# Revit family: CA_DWDI_CCW_BHD
name_source: partatom
category: Mechanical Equipment
units: mm (PartAtom-declared; Revit-internal decimal feet)

## family parameters
Always vertical = Yes
Cut with Voids When Loaded = No
OmniClass Number = 23.75.35.17
OmniClass Title = Fans
Part Type = Normal
Room Calculation Point = No
Round Connector Dimension = Use Radius
Shared = No
Work Plane-Based = No

## types (60) — shared parameters
0 = 0"
1" = 1"
1.5 = 1 1/2"
2" = 2"
2' = 24"
3" = 3"
4" = 4"
Manufacturer = Loren Cook Company
Model = CA DWDI
ONE EIGTH = 1/8"
URL = www.lorencook.com

## per-type parameters (varying)
- 120_CA-DWDI_CCW_BHD_CLASS_1: ((B+.25")/2)=8 31/32"; (D-A-.25")/2=1 9/16"; (G/5*3)+2"=10 1/16"; (M-(B+.25"))/2=1 7/8"; -((B+.25")/2)=-8 31/32"; -P=-28 11/16"; A=12 1/8"; A+.25"=12 3/8"; A/2=6 1/16"; B=17 11/16"; B+.25"=17 15/16"; B/2=8 27/32"; BHD_L=2 15/16"; D=15 1/2"; D/2=7 3/4"; E=21 1/16"; E/2=10 17/32"; F=25 3/4"; F-((D-A)/2)=24 1/16"; G=16"; G+((G/5*3)+2")=34 1/8"; G-(G/5*3)=1/4"; G-2.5"=14 9/16"; G/10*3=4 1/32"; G/5*3=8 1/16"; H=24 1/2"; H-1.5=23"; INLET=16 1/8"; INLET/2=8 1/16"; J=12 3/8"; K=22 1/2"; L=10 27/32"; M=21 11/16"; M/2=10 27/32"; N=5 3/4"; P=28 11/16"; P-N=-22 15/16"; P-N-M=1 1/4"; R=1 7/16"; R+R=2 7/8"; R/2=23/32"; S=19 15/16"; T=9 31/32"; Type Comments=Airfoil Centrifugal Blower Counter-Clockwise Bottom Horizontal Arrangement 3 Class 1; U=7 1/2"; V=18"; W=11/16"; W/2=11/32"; X=21 15/16"; X/2=10 31/32"
- 135_CA-DWDI_CCW_BHD_CLASS_1: ((B+.25")/2)=10 3/32"; (D-A-.25")/2=1 9/16"; (G/5*3)+2"=10 13/16"; (M-(B+.25"))/2=1 7/8"; -((B+.25")/2)=-10 3/32"; -P=-30 15/16"; A=13 5/8"; A+.25"=13 7/8"; A/2=6 13/16"; B=19 15/16"; B+.25"=20 3/16"; B/2=9 31/32"; BHD_L=2 5/16"; D=17"; D/2=8 1/2"; E=23 5/16"; E/2=11 21/32"; F=28"; F-((D-A)/2)=26 5/16"; G=17"; G+((G/5*3)+2")=36 5/8"; G-(G/5*3)=1/4"; G-2.5"=15 9/16"; G/10*3=4 13/32"; G/5*3=8 13/16"; H=27"; H-1.5=25 1/2"; INLET=17 5/8"; INLET/2=8 13/16"; J=13 7/8"; K=25"; L=11 31/32"; M=23 15/16"; M/2=11 31/32"; N=5 3/4"; P=30 15/16"; P-N=-25 3/16"; P-N-M=1 1/4"; R=1 7/16"; R+R=2 7/8"; R/2=23/32"; S=22 3/16"; T=11 3/32"; Type Comments=Airfoil Centrifugal Blower Counter-Clockwise Bottom Horizontal Arrangement 3 Class 1; U=8 1/2"; V=18"; W=11/16"; W/2=11/32"; X=24 3/16"; X/2=12 3/32"
- 150_CA-DWDI_CCW_BHD_CLASS_1: ((B+.25")/2)=11 1/8"; (D-A-.25")/2=1 9/16"; (G/5*3)+2"=11 9/16"; (M-(B+.25"))/2=1 7/8"; -((B+.25")/2)=-11 1/8"; -P=-34 1/4"; A=15 1/4"; A+.25"=15 1/2"; A/2=7 5/8"; B=22"; B+.25"=22 1/4"; B/2=11"; BHD_L=2 11/16"; D=18 5/8"; D/2=9 5/16"; E=25 3/8"; E/2=12 11/16"; F=31 3/16"; F-((D-A)/2)=29 1/2"; G=19"; G+((G/5*3)+2")=40 1/8"; G-(G/5*3)=1/4"; G-2.5"=17 5/16"; G/10*3=4 25/32"; G/5*3=9 9/16"; H=29"; H-1.5=27 1/2"; INLET=19 1/8"; INLET/2=9 9/16"; J=15 3/16"; K=26 7/8"; L=13"; M=26"; M/2=13"; N=6 5/8"; P=34 1/4"; P-N=-27 5/8"; P-N-M=1 5/8"; R=1 11/16"; R+R=3 3/8"; R/2=27/32"; S=24 1/4"; T=12 1/8"; Type Comments=Airfoil Centrifugal Blower Counter-Clockwise Bottom Horizontal Arrangement 3 Class 1; U=9"; V=18"; W=11/16"; W/2=11/32"; X=26 1/4"; X/2=13 1/8"
- 165_CA-DWDI_CCW_BHD_CLASS_1: ((B+.25")/2)=12 1/8"; (D-A-.25")/2=1 9/16"; (G/5*3)+2"=12 19/32"; (M-(B+.25"))/2=1 7/8"; -((B+.25")/2)=-12 1/8"; -P=-36 1/4"; A=16 15/16"; A+.25"=17 3/16"; A/2=8 15/32"; B=24"; B+.25"=24 1/4"; B/2=12"; BHD_L=3 1/16"; D=20 5/16"; D/2=10 5/32"; E=27 3/8"; E/2=13 11/16"; F=34 3/8"; F-((D-A)/2)=32 11/16"; G=21"; G+((G/5*3)+2")=44 3/16"; G-(G/5*3)=1/4"; G-2.5"=19 5/16"; G/10*3=5 5/16"; G/5*3=10 19/32"; H=31 1/2"; H-1.5=30"; INLET=21 3/16"; INLET/2=10 19/32"; J=16 5/8"; K=29 1/8"; L=14"; M=28"; M/2=14"; N=6 5/8"; P=36 1/4"; P-N=-29 5/8"; P-N-M=1 5/8"; R=1 11/16"; R+R=3 3/8"; R/2=27/32"; S=26 1/4"; T=13 1/8"; Type Comments=Airfoil Centrifugal Blower Counter-Clockwise Bottom Horizontal Arrangement 3 Class 1; U=10"; V=18"; W=11/16"; W/2=11/32"; X=28 1/4"; X/2=14 1/8"
- 180_CA-DWDI_CCW_BHD_CLASS_1: ((B+.25")/2)=13 5/32"; (D-A-.25")/2=1 9/16"; (G/5*3)+2"=13 11/32"; (M-(B+.25"))/2=1 7/8"; -((B+.25")/2)=-13 5/32"; -P=-38 13/16"; A=18 1/2"; A+.25"=18 3/4"; A/2=9 1/4"; B=26 1/16"; B+.25"=26 5/16"; B/2=13 1/32"; BHD_L=2 7/16"; D=21 7/8"; D/2=10 15/16"; E=29 7/16"; E/2=14 23/32"; F=36 5/8"; F-((D-A)/2)=34 15/16"; G=22"; G+((G/5*3)+2")=46 11/16"; G-(G/5*3)=1/4"; G-2.5"=20 5/16"; G/10*3=5 11/16"; G/5*3=11 11/32"; H=33 3/4"; H-1.5=32 1/4"; INLET=22 11/16"; INLET/2=11 11/32"; J=18 1/8"; K=30 7/8"; L=15 1/32"; M=30 1/16"; M/2=15 1/32"; N=7 1/8"; P=38 13/16"; P-N=-31 11/16"; P-N-M=1 5/8"; R=1 11/16"; R+R=3 3/8"; R/2=27/32"; S=28 5/16"; T=14 5/32"; Type Comments=Airfoil Centrifugal Blower Counter-Clockwise Bottom Horizontal Arrangement 3 Class 1; U=11"; V=18"; W=11/16"; W/2=11/32"; X=30 5/16"; X/2=15 5/32"
- 195_CA-DWDI_CCW_BHD_CLASS_1: ((B+.25")/2)=14 11/32"; (D-A-.25")/2=1 9/16"; (G/5*3)+2"=14 3/32"; (M-(B+.25"))/2=1 7/8"; -((B+.25")/2)=-14 11/32"; -P=-41 11/16"; A=19 1/2"; A+.25"=19 3/4"; A/2=9 3/4"; B=28 7/16"; B+.25"=28 11/16"; B/2=14 7/32"; BHD_L=2 13/16"; D=22 7/8"; D/2=11 7/16"; E=31 13/16"; E/2=15 29/32"; F=39 13/16"; F-((D-A)/2)=38 1/8"; G=24"; G+((G/5*3)+2")=50 3/16"; G-(G/5*3)=1/4"; G-2.5"=22 1/16"; G/10*3=6 1/16"; G/5*3=12 3/32"; H=36 1/4"; H-1.5=34 3/4"; INLET=24 3/16"; INLET/2=12 3/32"; J=19 7/16"; K=33"; L=16 7/32"; M=32 7/16"; M/2=16 7/32"; N=7 1/4"; P=41 11/16"; P-N=-34 7/16"; P-N-M=2"; R=1 15/16"; R+R=3 7/8"; R/2=31/32"; S=30 11/16"; T=15 11/32"; Type Comments=Airfoil Centrifugal Blower Counter-Clockwise Bottom Horizontal Arrangement 3 Class 1; U=11 1/2"; V=6"; W=11/16"; W/2=11/32"; X=32 11/16"; X/2=16 11/32"
- 210_CA-DWDI_CCW_BHD_CLASS_1: ((B+.25")/2)=15 5/16"; (D-A-.25")/2=1 9/16"; (G/5*3)+2"=14 31/32"; (M-(B+.25"))/2=1 7/8"; -((B+.25")/2)=-15 5/16"; -P=-44 1/8"; A=21 5/8"; A+.25"=21 7/8"; A/2=10 13/16"; B=30 3/8"; B+.25"=30 5/8"; B/2=15 3/16"; BHD_L=3 1/8"; D=25"; D/2=12 1/2"; E=33 3/4"; E/2=16 7/8"; F=43 1/16"; F-((D-A)/2)=41 3/8"; G=26"; G+((G/5*3)+2")=53 15/16"; G-(G/5*3)=1/4"; G-2.5"=24 1/16"; G/10*3=6 1/2"; G/5*3=12 31/32"; H=41"; H-1.5=39 1/2"; INLET=25 15/16"; INLET/2=12 31/32"; J=21"; K=38 7/8"; L=17 3/16"; M=34 3/8"; M/2=17 3/16"; N=7 7/8"; P=44 1/8"; P-N=-36 1/4"; P-N-M=1 7/8"; R=1 15/16"; R+R=3 7/8"; R/2=31/32"; S=32 5/8"; T=16 5/16"; Type Comments=Airfoil Centrifugal Blower Counter-Clockwise Bottom Horizontal Arrangement 3 Class 1; U=12"; V=7"; W=13/16"; W/2=13/32"; X=34 5/8"; X/2=17 5/16"
- 225_CA-DWDI_CCW_BHD_CLASS_1: ((B+.25")/2)=16 3/8"; (D-A-.25")/2=1 9/16"; (G/5*3)+2"=15 23/32"; (M-(B+.25"))/2=1 7/8"; -((B+.25")/2)=-16 3/8"; -P=-48 1/4"; A=23 3/16"; A+.25"=23 7/16"; A/2=11 19/32"; B=32 1/2"; B+.25"=32 3/4"; B/2=16 1/4"; BHD_L=3 1/2"; D=26 9/16"; D/2=13 9/32"; E=35 7/8"; E/2=17 15/16"; F=46 1/4"; F-((D-A)/2)=44 9/16"; G=28"; G+((G/5*3)+2")=57 7/16"; G-(G/5*3)=9/16"; G-2.5"=26 1/16"; G/10*3=6 7/8"; G/5*3=13 23/32"; H=43"; H-1.5=41 1/2"; INLET=27 7/16"; INLET/2=13 23/32"; J=22 3/8"; K=41 1/4"; L=18 1/4"; M=36 1/2"; M/2=18 1/4"; N=7 7/8"; P=48 1/4"; P-N=-40 3/8"; P-N-M=3 7/8"; R=1 15/16"; R+R=3 7/8"; R/2=31/32"; S=34 3/4"; T=17 3/8"; Type Comments=Airfoil Centrifugal Blower Counter-Clockwise Bottom Horizontal Arrangement 3 Class 1; U=12 1/2"; V=7 1/2"; W=13/16"; W/2=13/32"; X=36 3/4"; X/2=18 3/8"
- 245_CA-DWDI_CCW_BHD_CLASS_1: ((B+.25")/2)=17 21/32"; (D-A-.25")/2=1 9/16"; (G/5*3)+2"=16 23/32"; (M-(B+.25"))/2=1 7/8"; -((B+.25")/2)=-17 21/32"; -P=-49 13/16"; A=25 1/2"; A+.25"=25 3/4"; A/2=12 3/4"; B=35 1/16"; B+.25"=35 5/16"; B/2=17 17/32"; BHD_L=3 3/8"; D=28 7/8"; D/2=14 7/16"; E=38 7/16"; E/2=19 7/32"; F=49 7/8"; F-((D-A)/2)=48 3/16"; G=30"; G+((G/5*3)+2")=61 7/16"; G-(G/5*3)=9/16"; G-2.5"=27 13/16"; G/10*3=7 3/8"; G/5*3=14 23/32"; H=46"; H-1.5=44 1/2"; INLET=29 7/16"; INLET/2=14 23/32"; J=24 1/4"; K=43 5/8"; L=19 17/32"; M=39 1/16"; M/2=19 17/32"; N=8 5/8"; P=49 13/16"; P-N=-41 3/16"; P-N-M=2 1/8"; R=2 3/16"; R+R=4 3/8"; R/2=1 3/32"; S=37 5/16"; T=18 21/32"; Type Comments=Airfoil Centrifugal Blower Counter-Clockwise Bottom Horizontal Arrangement 3 Class 1; U=13 1/2"; V=8"; W=13/16"; W/2=13/32"; X=41 5/16"; X/2=20 21/32"
- 270_CA-DWDI_CCW_BHD_CLASS_1: ((B+.25")/2)=19 27/32"; (D-A-.25")/2=1 9/16"; (G/5*3)+2"=17 31/32"; (M-(B+.25"))/2=1 7/8"; -((B+.25")/2)=-19 27/32"; -P=-54 3/16"; A=27 1/2"; A+.25"=27 3/4"; A/2=13 3/4"; B=39 7/16"; B+.25"=39 11/16"; B/2=19 23/32"; BHD_L=3 5/8"; D=30 7/8"; D/2=15 7/16"; E=42 13/16"; E/2=21 13/32"; F=54 15/16"; F-((D-A)/2)=53 1/4"; G=33"; G+((G/5*3)+2")=66 15/16"; G-(G/5*3)=1 1/16"; G-2.5"=30 13/16"; G/10*3=8"; G/5*3=15 31/32"; H=50"; H-1.5=48 1/2"; INLET=31 15/16"; INLET/2=15 31/32"; J=26 5/8"; K=47 1/8"; L=21 23/32"; M=43 7/16"; M/2=21 23/32"; N=8 5/8"; P=54 3/16"; P-N=-45 9/16"; P-N-M=2 1/8"; R=2 3/16"; R+R=4 3/8"; R/2=1 3/32"; S=41 11/16"; T=20 27/32"; Type Comments=Airfoil Centrifugal Blower Counter-Clockwise Bottom Horizontal Arrangement 3 Class 1; U=15"; V=9"; W=13/16"; W/2=13/32"; X=45 11/16"; X/2=22 27/32"
- 300_CA-DWDI_CCW_BHD_CLASS_1: ((B+.25")/2)=21 5/8"; (D-A-.25")/2=1 19/32"; (G/5*3)+2"=19 15/32"; (M-(B+.25"))/2=1 7/8"; -((B+.25")/2)=-21 5/8"; -P=-58 1/2"; A=31 3/16"; A+.25"=31 7/16"; A/2=15 19/32"; B=43"; B+.25"=43 1/4"; B/2=21 1/2"; BHD_L=3 3/8"; D=34 5/8"; D/2=17 5/16"; E=46 7/16"; E/2=23 7/32"; F=60 3/8"; F-((D-A)/2)=58 21/32"; G=36"; G+((G/5*3)+2")=72 15/16"; G-(G/5*3)=1 1/16"; G-2.5"=33 9/16"; G/10*3=8 3/4"; G/5*3=17 15/32"; H=55 3/8"; H-1.5=53 7/8"; INLET=34 15/16"; INLET/2=17 15/32"; J=29 1/2"; K=52"; L=23 1/2"; M=47"; M/2=23 1/2"; N=9 1/4"; P=58 1/2"; P-N=-49 1/4"; P-N-M=2 1/4"; R=2 7/16"; R+R=4 7/8"; R/2=1 7/32"; S=45 1/4"; T=22 5/8"; Type Comments=Airfoil Centrifugal Blower Counter-Clockwise Bottom Horizontal Arrangement 3 Class 1; U=16 1/2"; V=10"; W=13/16"; W/2=13/32"; X=49 1/4"; X/2=24 5/8"
- 330_CA-DWDI_CCW_BHD_CLASS_1: ((B+.25")/2)=23 21/32"; (D-A-.25")/2=2 3/32"; (G/5*3)+2"=20 31/32"; (M-(B+.25"))/2=1 7/8"; -((B+.25")/2)=-23 21/32"; -P=-63 9/16"; A=34 1/2"; A+.25"=34 3/4"; A/2=17 1/4"; B=47 1/16"; B+.25"=47 5/16"; B/2=23 17/32"; BHD_L=3 1/8"; D=38 15/16"; D/2=19 15/32"; E=51 1/2"; E/2=25 3/4"; F=65 13/16"; F-((D-A)/2)=63 19/32"; G=39"; G+((G/5*3)+2")=78 15/16"; G-(G/5*3)=1 1/16"; G-2.5"=36 5/16"; G/10*3=9 1/2"; G/5*3=18 31/32"; H=60 3/4"; H-1.5=59 1/4"; INLET=37 15/16"; INLET/2=18 31/32"; J=32 5/16"; K=57"; L=25 17/32"; M=51 1/16"; M/2=25 17/32"; N=10 1/16"; P=63 9/16"; P-N=-53 1/2"; P-N-M=2 7/16"; R=2 11/16"; R+R=5 3/8"; R/2=1 11/32"; S=49 5/16"; T=24 21/32"; Type Comments=Airfoil Centrifugal Blower Counter-Clockwise Bottom Horizontal Arrangement 3 Class 1; U=18"; V=12"; W=13/16"; W/2=13/32"; X=53 7/16"; X/2=26 23/32"
- 365_CA-DWDI_CCW_BHD_CLASS_1: ((B+.25")/2)=26 7/32"; (D-A-.25")/2=2 3/32"; (G/5*3)+2"=22 23/32"; (M-(B+.25"))/2=1 7/8"; -((B+.25")/2)=-26 7/32"; -P=-69 5/16"; A=38 11/16"; A+.25"=38 15/16"; A/2=19 11/32"; B=52 3/16"; B+.25"=52 7/16"; B/2=26 3/32"; BHD_L=3 1/4"; D=43 1/8"; D/2=21 9/16"; E=56 5/8"; E/2=28 5/16"; F=72 5/8"; F-((D-A)/2)=70 13/32"; G=43"; G+((G/5*3)+2")=86 7/16"; G-(G/5*3)=1 9/16"; G-2.5"=40 13/16"; G/10*3=10 3/8"; G/5*3=20 23/32"; H=67"; H-1.5=65 1/2"; INLET=41 7/16"; INLET/2=20 23/32"; J=35 9/16"; K=63"; L=28 3/32"; M=56 3/16"; M/2=28 3/32"; N=10 5/16"; P=69 5/16"; P-N=-59"; P-N-M=2 13/16"; R=2 3/16"; R+R=4 3/8"; R/2=1 3/32"; S=54 7/16"; T=27 7/32"; Type Comments=Airfoil Centrifugal Blower Counter-Clockwise Bottom Horizontal Arrangement 3 Class 1; U=20"; V=13"; W=13/16"; W/2=13/32"; X=58 9/16"; X/2=29 9/32"
- 402_CA-DWDI_CCW_BHD_CLASS_1: ((B+.25")/2)=29 1/32"; (D-A-.25")/2=2 3/32"; (G/5*3)+2"=24 19/32"; (M-(B+.25"))/2=2 7/8"; -((B+.25")/2)=-29 1/32"; -P=-75 11/16"; A=41 3/4"; A+.25"=42"; A/2=20 7/8"; B=57 13/16"; B+.25"=58 1/16"; B/2=28 29/32"; BHD_L=3 1/4"; D=46 3/16"; D/2=23 3/32"; E=62 1/4"; E/2=31 1/8"; F=79 5/8"; F-((D-A)/2)=77 13/32"; G=47"; G+((G/5*3)+2")=94 3/16"; G-(G/5*3)=1 13/16"; G-2.5"=44 9/16"; G/10*3=11 5/16"; G/5*3=22 19/32"; H=73 7/8"; H-1.5=72 3/8"; INLET=45 3/16"; INLET/2=22 19/32"; J=39 3/16"; K=69"; L=31 29/32"; M=63 13/16"; M/2=31 29/32"; N=10"; P=75 11/16"; P-N=-65 11/16"; P-N-M=1 7/8"; R=2 7/16"; R+R=4 7/8"; R/2=1 7/32"; S=61 5/16"; T=30 21/32"; Type Comments=Airfoil Centrifugal Blower Counter-Clockwise Bottom Horizontal Arrangement 3 Class 1; U=22"; V=14"; W=1 1/16"; W/2=17/32"; X=65 3/16"; X/2=32 19/32"
- 445_CA-DWDI_CCW_BHD_CLASS_1: ((B+.25")/2)=32 1/4"; (D-A-.25")/2=2 3/32"; (G/5*3)+2"=26 23/32"; (M-(B+.25"))/2=2 7/8"; -((B+.25")/2)=-32 1/4"; -P=-82 5/8"; A=45 15/16"; A+.25"=46 3/16"; A/2=22 31/32"; B=64 1/4"; B+.25"=64 1/2"; B/2=32 1/8"; BHD_L=3 5/8"; D=50 3/8"; D/2=25 3/16"; E=68 11/16"; E/2=34 11/32"; F=88 1/8"; F-((D-A)/2)=85 29/32"; G=52"; G+((G/5*3)+2")=103 7/16"; G-(G/5*3)=2 9/16"; G-2.5"=49 9/16"; G/10*3=12 3/8"; G/5*3=24 23/32"; H=81 1/2"; H-1.5=80"; INLET=49 7/16"; INLET/2=24 23/32"; J=43 3/16"; K=77"; L=35 1/8"; M=70 1/4"; M/2=35 1/8"; N=10 5/8"; P=82 5/8"; P-N=-72"; P-N-M=1 3/4"; R=2 7/16"; R+R=4 7/8"; R/2=1 7/32"; S=67 3/4"; T=33 7/8"; Type Comments=Airfoil Centrifugal Blower Counter-Clockwise Bottom Horizontal Arrangement 3 Class 1; U=24"; V=16"; W=1 1/16"; W/2=17/32"; X=71 5/8"; X/2=35 13/16"
- 490_CA-DWDI_CCW_BHD_CLASS_1: ((B+.25")/2)=35 3/16"; (D-A-.25")/2=2 3/32"; (G/5*3)+2"=29 1/2"; (M-(B+.25"))/2=2 7/8"; -((B+.25")/2)=-35 3/16"; -P=-89 1/2"; A=51"; A+.25"=51 1/4"; A/2=25 1/2"; B=70 1/8"; B+.25"=70 3/8"; B/2=35 1/16"; BHD_L=3 3/4"; D=55 7/16"; D/2=27 23/32"; E=74 9/16"; E/2=37 9/32"; F=96 3/4"; F-((D-A)/2)=94 17/32"; G=57"; G+((G/5*3)+2")=114"; G-(G/5*3)=2"; G-2.5"=54 1/16"; G/10*3=13 3/4"; G/5*3=27 1/2"; H=89 3/4"; H-1.5=88 1/4"; INLET=55"; INLET/2=27 1/2"; J=47 9/16"; K=85"; L=38 1/16"; M=76 1/8"; M/2=38 1/16"; N=11 1/2"; P=89 1/2"; P-N=-78"; P-N-M=1 7/8"; R=2 15/16"; R+R=5 7/8"; R/2=1 15/32"; S=73 5/8"; T=36 13/16"; Type Comments=Airfoil Centrifugal Blower Counter-Clockwise Bottom Horizontal Arrangement 3 Class 1; U=26 1/2"; V=18"; W=1 1/16"; W/2=17/32"; X=77 1/2"; X/2=38 3/4"
- 540_CA-DWDI_CCW_BHD_CLASS_1: ((B+.25")/2)=39 3/32"; (D-A-.25")/2=2 3/32"; (G/5*3)+2"=32"; (M-(B+.25"))/2=2 7/8"; -((B+.25")/2)=-39 3/32"; -P=-98 5/16"; A=55 3/4"; A+.25"=56"; A/2=27 7/8"; B=77 15/16"; B+.25"=78 3/16"; B/2=38 31/32"; BHD_L=3 1/4"; D=60 3/16"; D/2=30 3/32"; E=82 3/8"; E/2=41 3/16"; F=105 13/16"; F-((D-A)/2)=103 19/32"; G=62"; G+((G/5*3)+2")=124"; G-(G/5*3)=2"; G-2.5"=58 9/16"; G/10*3=15"; G/5*3=30"; H=98 3/4"; H-1.5=97 1/4"; INLET=60"; INLET/2=30"; J=52 1/4"; K=94"; L=41 31/32"; M=83 15/16"; M/2=41 31/32"; N=12 7/16"; P=98 5/16"; P-N=-85 7/8"; P-N-M=1 15/16"; R=3 7/16"; R+R=6 7/8"; R/2=1 23/32"; S=81 7/16"; T=40 23/32"; Type Comments=Airfoil Centrifugal Blower Counter-Clockwise Bottom Horizontal Arrangement 3 Class 1; U=29"; V=20"; W=1 1/16"; W/2=17/32"; X=88 5/16"; X/2=44 5/32"
- 600_CA-DWDI_CCW_BHD_CLASS_1: ((B+.25")/2)=43 1/4"; (D-A-.25")/2=2 3/32"; (G/5*3)+2"=35"; (M-(B+.25"))/2=2 7/8"; -((B+.25")/2)=-43 1/4"; -P=-107 1/2"; A=62 3/16"; A+.25"=62 7/16"; A/2=31 3/32"; B=86 1/4"; B+.25"=86 1/2"; B/2=43 1/8"; BHD_L=3 3/4"; D=66 5/8"; D/2=33 5/16"; E=90 11/16"; E/2=45 11/32"; F=117 11/16"; F-((D-A)/2)=115 15/32"; G=69"; G+((G/5*3)+2")=137"; G-(G/5*3)=3"; G-2.5"=65 9/16"; G/10*3=16 1/2"; G/5*3=33"; H=109 5/8"; H-1.5=108 1/8"; INLET=66"; INLET/2=33"; J=57 15/16"; K=105"; L=46 1/8"; M=92 1/4"; M/2=46 1/8"; N=13"; P=107 1/2"; P-N=-94 1/2"; P-N-M=2 1/4"; R=3 7/16"; R+R=6 7/8"; R/2=1 23/32"; S=89 3/4"; T=44 7/8"; Type Comments=Airfoil Centrifugal Blower Counter-Clockwise Bottom Horizontal Arrangement 3 Class 1; U=32"; V=22"; W=1 1/16"; W/2=17/32"; X=96 5/8"; X/2=48 5/16"
- 660_CA-DWDI_CCW_BHD_CLASS_1: ((B+.25")/2)=47 9/16"; (D-A-.25")/2=2 3/32"; (G/5*3)+2"=38"; (M-(B+.25"))/2=2 7/8"; -((B+.25")/2)=-47 9/16"; -P=-117 7/8"; A=68 7/16"; A+.25"=68 11/16"; A/2=34 7/32"; B=94 7/8"; B+.25"=95 1/8"; B/2=47 7/16"; BHD_L=3 1/4"; D=72 7/8"; D/2=36 7/16"; E=99 5/16"; E/2=49 21/32"; F=128 9/16"; F-((D-A)/2)=126 11/32"; G=75"; G+((G/5*3)+2")=149"; G-(G/5*3)=3"; G-2.5"=71 1/16"; G/10*3=18"; G/5*3=36"; H=120 5/8"; H-1.5=119 1/8"; INLET=72"; INLET/2=36"; J=63 3/4"; K=116"; L=50 7/16"; M=100 7/8"; M/2=50 7/16"; N=14 13/16"; P=117 7/8"; P-N=-103 1/16"; P-N-M=2 3/16"; R=3 15/16"; R+R=7 7/8"; R/2=1 31/32"; S=98 3/8"; T=49 3/16"; Type Comments=Airfoil Centrifugal Blower Counter-Clockwise Bottom Horizontal Arrangement 3 Class 1; U=35"; V=25"; W=1 1/16"; W/2=17/32"; X=105 1/4"; X/2=52 5/8"
- 730 _CA-DWDI_CCW_BHD_CLASS_1: ((B+.25")/2)=52 1/2"; (D-A-.25")/2=2 3/32"; (G/5*3)+2"=41 1/2"; (M-(B+.25"))/2=2 7/8"; -((B+.25")/2)=-52 1/2"; -P=-129 1/4"; A=75 13/16"; A+.25"=76 1/16"; A/2=37 29/32"; B=104 3/4"; B+.25"=105"; B/2=52 3/8"; BHD_L=3 5/8"; D=80 1/4"; D/2=40 1/8"; E=109 3/16"; E/2=54 19/32"; F=142 1/4"; F-((D-A)/2)=140 1/32"; G=83"; G+((G/5*3)+2")=164"; G-(G/5*3)=4"; G-2.5"=78 9/16"; G/10*3=19 3/4"; G/5*3=39 1/2"; H=133 1/4"; H-1.5=131 3/4"; INLET=79"; INLET/2=39 1/2"; J=70 3/8"; K=129"; L=55 3/8"; M=110 3/4"; M/2=55 3/8"; N=16 5/16"; P=129 1/4"; P-N=-112 15/16"; P-N-M=2 3/16"; R=4 7/16"; R+R=8 7/8"; R/2=2 7/32"; S=108 1/4"; T=54 1/8"; Type Comments=Airfoil Centrifugal Blower Counter-Clockwise Bottom Horizontal Arrangement 3 Class 1; U=38 1/2"; V=28"; W=1 1/16"; W/2=17/32"; X=115 1/8"; X/2=57 9/16"
- 120_CA-DWDI_CCW_BHD_CLASS_2: ((B+.25")/2)=8 31/32"; (D-A-.25")/2=1 9/16"; (G/5*3)+2"=10 1/16"; (M-(B+.25"))/2=1 7/8"; -((B+.25")/2)=-8 31/32"; -P=-29 7/16"; A=12 1/8"; A+.25"=12 3/8"; A/2=6 1/16"; B=17 11/16"; B+.25"=17 15/16"; B/2=8 27/32"; BHD_L=2 15/16"; D=15 1/2"; D/2=7 3/4"; E=21 1/16"; E/2=10 17/32"; F=25 3/4"; F-((D-A)/2)=24 1/16"; G=16"; G+((G/5*3)+2")=34 1/8"; G-(G/5*3)=1/4"; G-2.5"=14 5/16"; G/10*3=4 1/32"; G/5*3=8 1/16"; H=24 1/2"; H-1.5=23"; INLET=16 1/8"; INLET/2=8 1/16"; J=12 3/8"; K=22 1/2"; L=10 27/32"; M=21 11/16"; M/2=10 27/32"; N=6 1/8"; P=29 7/16"; P-N=-23 5/16"; P-N-M=1 5/8"; R=1 11/16"; R+R=3 3/8"; R/2=27/32"; S=19 15/16"; T=9 31/32"; Type Comments=Airfoil Centrifugal Blower Counter-Clockwise Bottom Horizontal Arrangement 3 Class 2; U=7 1/2"; V=18"; W=11/16"; W/2=11/32"; X=21 15/16"; X/2=10 31/32"
- 120_CA-DWDI_CCW_BHD_CLASS_3: ((B+.25")/2)=8 31/32"; (D-A-.25")/2=1 9/16"; (G/5*3)+2"=10 1/16"; (M-(B+.25"))/2=1 7/8"; -((B+.25")/2)=-8 31/32"; -P=-29 15/16"; A=12 1/8"; A+.25"=12 3/8"; A/2=6 1/16"; B=17 11/16"; B+.25"=17 15/16"; B/2=8 27/32"; BHD_L=2 15/16"; D=15 1/2"; D/2=7 3/4"; E=21 1/16"; E/2=10 17/32"; F=25 3/4"; F-((D-A)/2)=24 1/16"; G=16"; G+((G/5*3)+2")=34 1/8"; G-(G/5*3)=1/4"; G-2.5"=14 1/16"; G/10*3=4 1/32"; G/5*3=8 1/16"; H=24 1/2"; H-1.5=23"; INLET=16 1/8"; INLET/2=8 1/16"; J=12 3/8"; K=22 1/2"; L=10 27/32"; M=21 11/16"; M/2=10 27/32"; N=6 3/8"; P=29 15/16"; P-N=-23 9/16"; P-N-M=1 7/8"; R=1 15/16"; R+R=3 7/8"; R/2=31/32"; S=19 15/16"; T=9 31/32"; Type Comments=Airfoil Centrifugal Blower Counter-Clockwise Bottom Horizontal Arrangement 3 Class 3; U=7 1/2"; V=18"; W=11/16"; W/2=11/32"; X=21 15/16"; X/2=10 31/32"
- 135_CA-DWDI_CCW_BHD_CLASS_2: ((B+.25")/2)=10 3/32"; (D-A-.25")/2=1 9/16"; (G/5*3)+2"=10 13/16"; (M-(B+.25"))/2=1 7/8"; -((B+.25")/2)=-10 3/32"; -P=-31 11/16"; A=13 5/8"; A+.25"=13 7/8"; A/2=6 13/16"; B=19 15/16"; B+.25"=20 3/16"; B/2=9 31/32"; BHD_L=2 5/16"; D=17"; D/2=8 1/2"; E=23 5/16"; E/2=11 21/32"; F=28"; F-((D-A)/2)=26 5/16"; G=17"; G+((G/5*3)+2")=36 5/8"; G-(G/5*3)=1/4"; G-2.5"=15 5/16"; G/10*3=4 13/32"; G/5*3=8 13/16"; H=27"; H-1.5=25 1/2"; INLET=17 5/8"; INLET/2=8 13/16"; J=13 7/8"; K=25"; L=11 31/32"; M=23 15/16"; M/2=11 31/32"; N=6 1/8"; P=31 11/16"; P-N=-25 9/16"; P-N-M=1 5/8"; R=1 11/16"; R+R=3 3/8"; R/2=27/32"; S=22 3/16"; T=11 3/32"; Type Comments=Airfoil Centrifugal Blower Counter-Clockwise Bottom Horizontal Arrangement 3 Class 2; U=8 1/2"; V=18"; W=11/16"; W/2=11/32"; X=24 3/16"; X/2=12 3/32"
- 135_CA-DWDI_CCW_BHD_CLASS_3: ((B+.25")/2)=10 3/32"; (D-A-.25")/2=1 9/16"; (G/5*3)+2"=10 13/16"; (M-(B+.25"))/2=1 7/8"; -((B+.25")/2)=-10 3/32"; -P=-32 11/16"; A=13 5/8"; A+.25"=13 7/8"; A/2=6 13/16"; B=19 15/16"; B+.25"=20 3/16"; B/2=9 31/32"; BHD_L=2 5/16"; D=17"; D/2=8 1/2"; E=23 5/16"; E/2=11 21/32"; F=28"; F-((D-A)/2)=26 5/16"; G=17"; G+((G/5*3)+2")=36 5/8"; G-(G/5*3)=1/4"; G-2.5"=14 13/16"; G/10*3=4 13/32"; G/5*3=8 13/16"; H=27"; H-1.5=25 1/2"; INLET=17 5/8"; INLET/2=8 13/16"; J=13 7/8"; K=25"; L=11 31/32"; M=23 15/16"; M/2=11 31/32"; N=6 5/8"; P=32 11/16"; P-N=-26 1/16"; P-N-M=2 1/8"; R=2 3/16"; R+R=4 3/8"; R/2=1 3/32"; S=22 3/16"; T=11 3/32"; Type Comments=Airfoil Centrifugal Blower Counter-Clockwise Bottom Horizontal Arrangement 3 Class 3; U=8 1/2"; V=18"; W=11/16"; W/2=11/32"; X=24 3/16"; X/2=12 3/32"
- 150_CA-DWDI_CCW_BHD_CLASS_2: ((B+.25")/2)=11 1/8"; (D-A-.25")/2=1 9/16"; (G/5*3)+2"=11 9/16"; (M-(B+.25"))/2=1 7/8"; -((B+.25")/2)=-11 1/8"; -P=-34 3/4"; A=15 1/4"; A+.25"=15 1/2"; A/2=7 5/8"; B=22"; B+.25"=22 1/4"; B/2=11"; BHD_L=2 11/16"; D=18 5/8"; D/2=9 5/16"; E=25 3/8"; E/2=12 11/16"; F=31 3/16"; F-((D-A)/2)=29 1/2"; G=19"; G+((G/5*3)+2")=40 1/8"; G-(G/5*3)=1/4"; G-2.5"=17 1/16"; G/10*3=4 25/32"; G/5*3=9 9/16"; H=29"; H-1.5=27 1/2"; INLET=19 1/8"; INLET/2=9 9/16"; J=15 3/16"; K=26 7/8"; L=13"; M=26"; M/2=13"; N=6 7/8"; P=34 3/4"; P-N=-27 7/8"; P-N-M=1 7/8"; R=1 15/16"; R+R=3 7/8"; R/2=31/32"; S=24 1/4"; T=12 1/8"; Type Comments=Airfoil Centrifugal Blower Counter-Clockwise Bottom Horizontal Arrangement 3 Class 2; U=9"; V=18"; W=11/16"; W/2=11/32"; X=26 1/4"; X/2=13 1/8"
- 150_CA-DWDI_CCW_BHD_CLASS_3: ((B+.25")/2)=11 1/8"; (D-A-.25")/2=1 9/16"; (G/5*3)+2"=11 9/16"; (M-(B+.25"))/2=1 7/8"; -((B+.25")/2)=-11 1/8"; -P=-35 1/2"; A=15 1/4"; A+.25"=15 1/2"; A/2=7 5/8"; B=22"; B+.25"=22 1/4"; B/2=11"; BHD_L=2 11/16"; D=18 5/8"; D/2=9 5/16"; E=25 3/8"; E/2=12 11/16"; F=31 3/16"; F-((D-A)/2)=29 1/2"; G=19"; G+((G/5*3)+2")=40 1/8"; G-(G/5*3)=1/4"; G-2.5"=16 9/16"; G/10*3=4 25/32"; G/5*3=9 9/16"; H=29"; H-1.5=27 1/2"; INLET=19 1/8"; INLET/2=9 9/16"; J=15 3/16"; K=26 7/8"; L=13"; M=26"; M/2=13"; N=7 1/4"; P=35 1/2"; P-N=-28 1/4"; P-N-M=2 1/4"; R=2 7/16"; R+R=4 7/8"; R/2=1 7/32"; S=24 1/4"; T=12 1/8"; Type Comments=Airfoil Centrifugal Blower Counter-Clockwise Bottom Horizontal Arrangement 3 Class 3; U=9"; V=18"; W=11/16"; W/2=11/32"; X=26 1/4"; X/2=13 1/8"
- 165_CA-DWDI_CCW_BHD_CLASS_2: ((B+.25")/2)=12 1/8"; (D-A-.25")/2=1 9/16"; (G/5*3)+2"=12 19/32"; (M-(B+.25"))/2=1 7/8"; -((B+.25")/2)=-12 1/8"; -P=-36 3/4"; A=16 15/16"; A+.25"=17 3/16"; A/2=8 15/32"; B=24"; B+.25"=24 1/4"; B/2=12"; BHD_L=3 1/16"; D=20 5/16"; D/2=10 5/32"; E=27 3/8"; E/2=13 11/16"; F=34 3/8"; F-((D-A)/2)=32 11/16"; G=21"; G+((G/5*3)+2")=44 3/16"; G-(G/5*3)=1/4"; G-2.5"=19 1/16"; G/10*3=5 5/16"; G/5*3=10 19/32"; H=31 1/2"; H-1.5=30"; INLET=21 3/16"; INLET/2=10 19/32"; J=16 5/8"; K=29 1/8"; L=14"; M=28"; M/2=14"; N=6 7/8"; P=36 3/4"; P-N=-29 7/8"; P-N-M=1 7/8"; R=1 15/16"; R+R=3 7/8"; R/2=31/32"; S=26 1/4"; T=13 1/8"; Type Comments=Airfoil Centrifugal Blower Counter-Clockwise Bottom Horizontal Arrangement 3 Class 2; U=10"; V=18"; W=11/16"; W/2=11/32"; X=28 1/4"; X/2=14 1/8"
- 165_CA-DWDI_CCW_BHD_CLASS_3: ((B+.25")/2)=12 1/8"; (D-A-.25")/2=1 9/16"; (G/5*3)+2"=12 19/32"; (M-(B+.25"))/2=1 7/8"; -((B+.25")/2)=-12 1/8"; -P=-37 1/2"; A=16 15/16"; A+.25"=17 3/16"; A/2=8 15/32"; B=24"; B+.25"=24 1/4"; B/2=12"; BHD_L=3 1/16"; D=20 5/16"; D/2=10 5/32"; E=27 3/8"; E/2=13 11/16"; F=34 3/8"; F-((D-A)/2)=32 11/16"; G=21"; G+((G/5*3)+2")=44 3/16"; G-(G/5*3)=1/4"; G-2.5"=18 9/16"; G/10*3=5 5/16"; G/5*3=10 19/32"; H=31 1/2"; H-1.5=30"; INLET=21 3/16"; INLET/2=10 19/32"; J=16 5/8"; K=29 1/8"; L=14"; M=28"; M/2=14"; N=7 3/16"; P=37 1/2"; P-N=-30 5/16"; P-N-M=2 5/16"; R=2 7/16"; R+R=4 7/8"; R/2=1 7/32"; S=26 1/4"; T=13 1/8"; Type Comments=Airfoil Centrifugal Blower Counter-Clockwise Bottom Horizontal Arrangement 3 Class 3; U=10"; V=18"; W=11/16"; W/2=11/32"; X=28 1/4"; X/2=14 1/8"
- 180_CA-DWDI_CCW_BHD_CLASS_2: ((B+.25")/2)=13 5/32"; (D-A-.25")/2=1 9/16"; (G/5*3)+2"=13 11/32"; (M-(B+.25"))/2=1 7/8"; -((B+.25")/2)=-13 5/32"; -P=-39 5/16"; A=18 1/2"; A+.25"=18 3/4"; A/2=9 1/4"; B=26 1/16"; B+.25"=26 5/16"; B/2=13 1/32"; BHD_L=2 7/16"; D=21 7/8"; D/2=10 15/16"; E=29 7/16"; E/2=14 23/32"; F=36 5/8"; F-((D-A)/2)=34 15/16"; G=22"; G+((G/5*3)+2")=46 11/16"; G-(G/5*3)=1/4"; G-2.5"=20 1/16"; G/10*3=5 11/16"; G/5*3=11 11/32"; H=33 3/4"; H-1.5=32 1/4"; INLET=22 11/16"; INLET/2=11 11/32"; J=18 1/8"; K=30 7/8"; L=15 1/32"; M=30 1/16"; M/2=15 1/32"; N=7 3/8"; P=39 5/16"; P-N=-31 15/16"; P-N-M=1 7/8"; R=1 15/16"; R+R=3 7/8"; R/2=31/32"; S=28 5/16"; T=14 5/32"; Type Comments=Airfoil Centrifugal Blower Counter-Clockwise Bottom Horizontal Arrangement 3 Class 2; U=11"; V=18"; W=11/16"; W/2=11/32"; X=30 5/16"; X/2=15 5/32"
- 180_CA-DWDI_CCW_BHD_CLASS_3: ((B+.25")/2)=13 5/32"; (D-A-.25")/2=1 9/16"; (G/5*3)+2"=13 11/32"; (M-(B+.25"))/2=1 7/8"; -((B+.25")/2)=-13 5/32"; -P=-40 1/16"; A=18 1/2"; A+.25"=18 3/4"; A/2=9 1/4"; B=26 1/16"; B+.25"=26 5/16"; B/2=13 1/32"; BHD_L=2 7/16"; D=21 7/8"; D/2=10 15/16"; E=29 7/16"; E/2=14 23/32"; F=36 5/8"; F-((D-A)/2)=34 15/16"; G=22"; G+((G/5*3)+2")=46 11/16"; G-(G/5*3)=1/4"; G-2.5"=19 9/16"; G/10*3=5 11/16"; G/5*3=11 11/32"; H=33 3/4"; H-1.5=32 1/4"; INLET=22 11/16"; INLET/2=11 11/32"; J=18 1/8"; K=30 7/8"; L=15 1/32"; M=30 1/16"; M/2=15 1/32"; N=7 3/4"; P=40 1/16"; P-N=-32 5/16"; P-N-M=2 1/4"; R=2 7/16"; R+R=4 7/8"; R/2=1 7/32"; S=28 5/16"; T=14 5/32"; Type Comments=Airfoil Centrifugal Blower Counter-Clockwise Bottom Horizontal Arrangement 3 Class 3; U=11"; V=18"; W=11/16"; W/2=11/32"; X=30 5/16"; X/2=15 5/32"
- 195_CA-DWDI_CCW_BHD_CLASS_2: ((B+.25")/2)=14 11/32"; (D-A-.25")/2=1 9/16"; (G/5*3)+2"=14 3/32"; (M-(B+.25"))/2=1 7/8"; -((B+.25")/2)=-14 11/32"; -P=-42 3/16"; A=19 1/2"; A+.25"=19 3/4"; A/2=9 3/4"; B=28 7/16"; B+.25"=28 11/16"; B/2=14 7/32"; BHD_L=2 13/16"; D=22 7/8"; D/2=11 7/16"; E=31 13/16"; E/2=15 29/32"; F=39 13/16"; F-((D-A)/2)=38 1/8"; G=24"; G+((G/5*3)+2")=50 3/16"; G-(G/5*3)=1/4"; G-2.5"=21 13/16"; G/10*3=6 1/16"; G/5*3=12 3/32"; H=36 1/4"; H-1.5=34 3/4"; INLET=24 3/16"; INLET/2=12 3/32"; J=19 7/16"; K=33"; L=16 7/32"; M=32 7/16"; M/2=16 7/32"; N=7 5/8"; P=42 3/16"; P-N=-34 9/16"; P-N-M=2 1/8"; R=2 3/16"; R+R=4 3/8"; R/2=1 3/32"; S=30 11/16"; T=15 11/32"; Type Comments=Airfoil Centrifugal Blower Counter-Clockwise Bottom Horizontal Arrangement 3 Class 2; U=11 1/2"; V=6"; W=11/16"; W/2=11/32"; X=32 11/16"; X/2=16 11/32"
- 195_CA-DWDI_CCW_BHD_CLASS_3: ((B+.25")/2)=14 11/32"; (D-A-.25")/2=1 9/16"; (G/5*3)+2"=14 3/32"; (M-(B+.25"))/2=1 7/8"; -((B+.25")/2)=-14 11/32"; -P=-42 15/16"; A=19 1/2"; A+.25"=19 3/4"; A/2=9 3/4"; B=28 7/16"; B+.25"=28 11/16"; B/2=14 7/32"; BHD_L=2 13/16"; D=22 7/8"; D/2=11 7/16"; E=31 13/16"; E/2=15 29/32"; F=39 13/16"; F-((D-A)/2)=38 1/8"; G=24"; G+((G/5*3)+2")=50 3/16"; G-(G/5*3)=1/4"; G-2.5"=21 5/16"; G/10*3=6 1/16"; G/5*3=12 3/32"; H=36 1/4"; H-1.5=34 3/4"; INLET=24 3/16"; INLET/2=12 3/32"; J=19 7/16"; K=33"; L=16 7/32"; M=32 7/16"; M/2=16 7/32"; N=8"; P=42 15/16"; P-N=-34 15/16"; P-N-M=2 1/2"; R=2 11/16"; R+R=5 3/8"; R/2=1 11/32"; S=30 11/16"; T=15 11/32"; Type Comments=Airfoil Centrifugal Blower Counter-Clockwise Bottom Horizontal Arrangement 3 Class 3; U=11 1/2"; V=6"; W=11/16"; W/2=11/32"; X=32 11/16"; X/2=16 11/32"
- 210_CA-DWDI_CCW_BHD_CLASS_2: ((B+.25")/2)=15 5/16"; (D-A-.25")/2=1 9/16"; (G/5*3)+2"=14 31/32"; (M-(B+.25"))/2=1 7/8"; -((B+.25")/2)=-15 5/16"; -P=-44 5/8"; A=21 5/8"; A+.25"=21 7/8"; A/2=10 13/16"; B=30 3/8"; B+.25"=30 5/8"; B/2=15 3/16"; BHD_L=3 1/8"; D=25"; D/2=12 1/2"; E=33 3/4"; E/2=16 7/8"; F=43 1/16"; F-((D-A)/2)=41 3/8"; G=26"; G+((G/5*3)+2")=53 15/16"; G-(G/5*3)=1/4"; G-2.5"=23 13/16"; G/10*3=6 1/2"; G/5*3=12 31/32"; H=41"; H-1.5=39 1/2"; INLET=25 15/16"; INLET/2=12 31/32"; J=21"; K=38 7/8"; L=17 3/16"; M=34 3/8"; M/2=17 3/16"; N=8 1/8"; P=44 5/8"; P-N=-36 1/2"; P-N-M=2 1/8"; R=2 3/16"; R+R=4 3/8"; R/2=1 3/32"; S=32 5/8"; T=16 5/16"; Type Comments=Airfoil Centrifugal Blower Counter-Clockwise Bottom Horizontal Arrangement 3 Class 2; U=12"; V=7"; W=13/16"; W/2=13/32"; X=34 5/8"; X/2=17 5/16"
- 210_CA-DWDI_CCW_BHD_CLASS_3: ((B+.25")/2)=15 5/16"; (D-A-.25")/2=1 9/16"; (G/5*3)+2"=14 31/32"; (M-(B+.25"))/2=1 7/8"; -((B+.25")/2)=-15 5/16"; -P=-45 3/8"; A=21 5/8"; A+.25"=21 7/8"; A/2=10 13/16"; B=30 3/8"; B+.25"=30 5/8"; B/2=15 3/16"; BHD_L=3 1/8"; D=25"; D/2=12 1/2"; E=33 3/4"; E/2=16 7/8"; F=43 1/16"; F-((D-A)/2)=41 3/8"; G=26"; G+((G/5*3)+2")=53 15/16"; G-(G/5*3)=1/4"; G-2.5"=23 5/16"; G/10*3=6 1/2"; G/5*3=12 31/32"; H=41"; H-1.5=39 1/2"; INLET=25 15/16"; INLET/2=12 31/32"; J=21"; K=38 7/8"; L=17 3/16"; M=34 3/8"; M/2=17 3/16"; N=8 1/2"; P=45 3/8"; P-N=-36 7/8"; P-N-M=2 1/2"; R=2 11/16"; R+R=5 3/8"; R/2=1 11/32"; S=32 5/8"; T=16 5/16"; Type Comments=Airfoil Centrifugal Blower Counter-Clockwise Bottom Horizontal Arrangement 3 Class 3; U=12"; V=7"; W=13/16"; W/2=13/32"; X=34 5/8"; X/2=17 5/16"
- 225_CA-DWDI_CCW_BHD_CLASS_2: ((B+.25")/2)=16 3/8"; (D-A-.25")/2=1 9/16"; (G/5*3)+2"=15 23/32"; (M-(B+.25"))/2=1 7/8"; -((B+.25")/2)=-16 3/8"; -P=-47"; A=23 3/16"; A+.25"=23 7/16"; A/2=11 19/32"; B=32 1/2"; B+.25"=32 3/4"; B/2=16 1/4"; BHD_L=3 1/2"; D=26 9/16"; D/2=13 9/32"; E=35 7/8"; E/2=17 15/16"; F=46 1/4"; F-((D-A)/2)=44 9/16"; G=28"; G+((G/5*3)+2")=57 7/16"; G-(G/5*3)=9/16"; G-2.5"=25 9/16"; G/10*3=6 7/8"; G/5*3=13 23/32"; H=43"; H-1.5=41 1/2"; INLET=27 7/16"; INLET/2=13 23/32"; J=22 3/8"; K=41 1/4"; L=18 1/4"; M=36 1/2"; M/2=18 1/4"; N=8 1/4"; P=47"; P-N=-38 3/4"; P-N-M=2 1/4"; R=2 7/16"; R+R=4 7/8"; R/2=1 7/32"; S=34 3/4"; T=17 3/8"; Type Comments=Airfoil Centrifugal Blower Counter-Clockwise Bottom Horizontal Arrangement 3 Class 2; U=12 1/2"; V=7 1/2"; W=13/16"; W/2=13/32"; X=36 3/4"; X/2=18 3/8"
- 225_CA-DWDI_CCW_BHD_CLASS_3: ((B+.25")/2)=16 3/8"; (D-A-.25")/2=1 9/16"; (G/5*3)+2"=15 23/32"; (M-(B+.25"))/2=1 7/8"; -((B+.25")/2)=-16 3/8"; -P=-47 1/2"; A=23 3/16"; A+.25"=23 7/16"; A/2=11 19/32"; B=32 1/2"; B+.25"=32 3/4"; B/2=16 1/4"; BHD_L=3 1/2"; D=26 9/16"; D/2=13 9/32"; E=35 7/8"; E/2=17 15/16"; F=46 1/4"; F-((D-A)/2)=44 9/16"; G=28"; G+((G/5*3)+2")=57 7/16"; G-(G/5*3)=9/16"; G-2.5"=25 1/16"; G/10*3=6 7/8"; G/5*3=13 23/32"; H=43"; H-1.5=41 1/2"; INLET=27 7/16"; INLET/2=13 23/32"; J=22 3/8"; K=41 1/4"; L=18 1/4"; M=36 1/2"; M/2=18 1/4"; N=8 1/2"; P=47 1/2"; P-N=-39"; P-N-M=2 1/2"; R=2 15/16"; R+R=5 7/8"; R/2=1 15/32"; S=34 3/4"; T=17 3/8"; Type Comments=Airfoil Centrifugal Blower Counter-Clockwise Bottom Horizontal Arrangement 3 Class 3; U=12 1/2"; V=7 1/2"; W=13/16"; W/2=13/32"; X=36 3/4"; X/2=18 3/8"
- 245_CA-DWDI_CCW_BHD_CLASS_2: ((B+.25")/2)=17 21/32"; (D-A-.25")/2=1 9/16"; (G/5*3)+2"=16 23/32"; (M-(B+.25"))/2=1 7/8"; -((B+.25")/2)=-17 21/32"; -P=-50 1/16"; A=25 1/2"; A+.25"=25 3/4"; A/2=12 3/4"; B=35 1/16"; B+.25"=35 5/16"; B/2=17 17/32"; BHD_L=3 3/8"; D=28 7/8"; D/2=14 7/16"; E=38 7/16"; E/2=19 7/32"; F=49 7/8"; F-((D-A)/2)=48 3/16"; G=30"; G+((G/5*3)+2")=61 7/16"; G-(G/5*3)=9/16"; G-2.5"=27 9/16"; G/10*3=7 3/8"; G/5*3=14 23/32"; H=46"; H-1.5=44 1/2"; INLET=29 7/16"; INLET/2=14 23/32"; J=24 1/4"; K=43 5/8"; L=19 17/32"; M=39 1/16"; M/2=19 17/32"; N=8 3/4"; P=50 1/16"; P-N=-41 5/16"; P-N-M=2 1/4"; R=2 7/16"; R+R=4 7/8"; R/2=1 7/32"; S=37 5/16"; T=18 21/32"; Type Comments=Airfoil Centrifugal Blower Counter-Clockwise Bottom Horizontal Arrangement 3 Class 2; U=13 1/2"; V=8"; W=13/16"; W/2=13/32"; X=41 5/16"; X/2=20 21/32"
- 245_CA-DWDI_CCW_BHD_CLASS_3: ((B+.25")/2)=17 21/32"; (D-A-.25")/2=1 9/16"; (G/5*3)+2"=16 23/32"; (M-(B+.25"))/2=1 7/8"; -((B+.25")/2)=-17 21/32"; -P=-50 11/16"; A=25 1/2"; A+.25"=25 3/4"; A/2=12 3/4"; B=35 1/16"; B+.25"=35 5/16"; B/2=17 17/32"; BHD_L=3 3/8"; D=28 7/8"; D/2=14 7/16"; E=38 7/16"; E/2=19 7/32"; F=49 7/8"; F-((D-A)/2)=48 3/16"; G=30"; G+((G/5*3)+2")=61 7/16"; G-(G/5*3)=9/16"; G-2.5"=27 13/16"; G/10*3=7 3/8"; G/5*3=14 23/32"; H=46"; H-1.5=44 1/2"; INLET=29 7/16"; INLET/2=14 23/32"; J=24 1/4"; K=43 5/8"; L=19 17/32"; M=39 1/16"; M/2=19 17/32"; N=8 3/4"; P=50 11/16"; P-N=-41 15/16"; P-N-M=2 7/8"; R=2 3/16"; R+R=4 3/8"; R/2=1 3/32"; S=37 5/16"; T=18 21/32"; Type Comments=Airfoil Centrifugal Blower Counter-Clockwise Bottom Horizontal Arrangement 3 Class 3; U=13 1/2"; V=8"; W=13/16"; W/2=13/32"; X=41 5/16"; X/2=20 21/32"
- 270_CA-DWDI_CCW_BHD_CLASS_2: ((B+.25")/2)=19 27/32"; (D-A-.25")/2=1 9/16"; (G/5*3)+2"=17 31/32"; (M-(B+.25"))/2=1 7/8"; -((B+.25")/2)=-19 27/32"; -P=-54 15/16"; A=27 1/2"; A+.25"=27 3/4"; A/2=13 3/4"; B=39 7/16"; B+.25"=39 11/16"; B/2=19 23/32"; BHD_L=3 5/8"; D=30 7/8"; D/2=15 7/16"; E=42 13/16"; E/2=21 13/32"; F=54 15/16"; F-((D-A)/2)=53 1/4"; G=33"; G+((G/5*3)+2")=66 15/16"; G-(G/5*3)=1 1/16"; G-2.5"=30 5/16"; G/10*3=8"; G/5*3=15 31/32"; H=50"; H-1.5=48 1/2"; INLET=31 15/16"; INLET/2=15 31/32"; J=26 5/8"; K=47 1/8"; L=21 23/32"; M=43 7/16"; M/2=21 23/32"; N=9"; P=54 15/16"; P-N=-45 15/16"; P-N-M=2 1/2"; R=2 11/16"; R+R=5 3/8"; R/2=1 11/32"; S=41 11/16"; T=20 27/32"; Type Comments=Airfoil Centrifugal Blower Counter-Clockwise Bottom Horizontal Arrangement 3 Class 2; U=15"; V=9"; W=13/16"; W/2=13/32"; X=45 11/16"; X/2=22 27/32"
- 270_CA-DWDI_CCW_BHD_CLASS_3: ((B+.25")/2)=19 27/32"; (D-A-.25")/2=1 9/16"; (G/5*3)+2"=17 31/32"; (M-(B+.25"))/2=1 7/8"; -((B+.25")/2)=-19 27/32"; -P=-55 1/16"; A=27 1/2"; A+.25"=27 3/4"; A/2=13 3/4"; B=39 7/16"; B+.25"=39 11/16"; B/2=19 23/32"; BHD_L=3 5/8"; D=30 7/8"; D/2=15 7/16"; E=42 13/16"; E/2=21 13/32"; F=54 15/16"; F-((D-A)/2)=53 1/4"; G=33"; G+((G/5*3)+2")=66 15/16"; G-(G/5*3)=1 1/16"; G-2.5"=30 13/16"; G/10*3=8"; G/5*3=15 31/32"; H=50"; H-1.5=48 1/2"; INLET=31 15/16"; INLET/2=15 31/32"; J=26 5/8"; K=47 1/8"; L=21 23/32"; M=43 7/16"; M/2=21 23/32"; N=8 3/4"; P=55 1/16"; P-N=-46 5/16"; P-N-M=2 7/8"; R=2 3/16"; R+R=4 3/8"; R/2=1 3/32"; S=41 11/16"; T=20 27/32"; Type Comments=Airfoil Centrifugal Blower Counter-Clockwise Bottom Horizontal Arrangement 3 Class 3; U=15"; V=9"; W=13/16"; W/2=13/32"; X=45 11/16"; X/2=22 27/32"
- 300_CA-DWDI_CCW_BHD_CLASS_2: ((B+.25")/2)=21 5/8"; (D-A-.25")/2=1 19/32"; (G/5*3)+2"=19 15/32"; (M-(B+.25"))/2=1 7/8"; -((B+.25")/2)=-21 5/8"; -P=-59"; A=31 3/16"; A+.25"=31 7/16"; A/2=15 19/32"; B=43"; B+.25"=43 1/4"; B/2=21 1/2"; BHD_L=3 3/8"; D=34 5/8"; D/2=17 5/16"; E=46 7/16"; E/2=23 7/32"; F=60 3/8"; F-((D-A)/2)=58 21/32"; G=36"; G+((G/5*3)+2")=72 15/16"; G-(G/5*3)=1 1/16"; G-2.5"=33 5/16"; G/10*3=8 3/4"; G/5*3=17 15/32"; H=55 3/8"; H-1.5=53 7/8"; INLET=34 15/16"; INLET/2=17 15/32"; J=29 1/2"; K=52"; L=23 1/2"; M=47"; M/2=23 1/2"; N=9 1/2"; P=59"; P-N=-49 1/2"; P-N-M=2 1/2"; R=2 11/16"; R+R=5 3/8"; R/2=1 11/32"; S=45 1/4"; T=22 5/8"; Type Comments=Airfoil Centrifugal Blower Counter-Clockwise Bottom Horizontal Arrangement 3 Class 2; U=16 1/2"; V=10"; W=13/16"; W/2=13/32"; X=49 1/4"; X/2=24 5/8"
- 300_CA-DWDI_CCW_BHD_CLASS_3: ((B+.25")/2)=21 5/8"; (D-A-.25")/2=1 19/32"; (G/5*3)+2"=19 15/32"; (M-(B+.25"))/2=1 7/8"; -((B+.25")/2)=-21 5/8"; -P=-59 3/8"; A=31 3/16"; A+.25"=31 7/16"; A/2=15 19/32"; B=43"; B+.25"=43 1/4"; B/2=21 1/2"; BHD_L=3 3/8"; D=34 5/8"; D/2=17 5/16"; E=46 7/16"; E/2=23 7/32"; F=60 3/8"; F-((D-A)/2)=58 21/32"; G=36"; G+((G/5*3)+2")=72 15/16"; G-(G/5*3)=1 1/16"; G-2.5"=33 9/16"; G/10*3=8 3/4"; G/5*3=17 15/32"; H=55 3/8"; H-1.5=53 7/8"; INLET=34 15/16"; INLET/2=17 15/32"; J=29 1/2"; K=52"; L=23 1/2"; M=47"; M/2=23 1/2"; N=9 1/2"; P=59 3/8"; P-N=-49 7/8"; P-N-M=2 7/8"; R=2 7/16"; R+R=4 7/8"; R/2=1 7/32"; S=45 1/4"; T=22 5/8"; Type Comments=Airfoil Centrifugal Blower Counter-Clockwise Bottom Horizontal Arrangement 3 Class 3; U=16 1/2"; V=10"; W=13/16"; W/2=13/32"; X=49 1/4"; X/2=24 5/8"
- 330_CA-DWDI_CCW_BHD_CLASS_2: ((B+.25")/2)=23 21/32"; (D-A-.25")/2=2 3/32"; (G/5*3)+2"=20 31/32"; (M-(B+.25"))/2=1 7/8"; -((B+.25")/2)=-23 21/32"; -P=-63 11/16"; A=34 1/2"; A+.25"=34 3/4"; A/2=17 1/4"; B=47 1/16"; B+.25"=47 5/16"; B/2=23 17/32"; BHD_L=3 1/8"; D=38 15/16"; D/2=19 15/32"; E=51 1/2"; E/2=25 3/4"; F=65 13/16"; F-((D-A)/2)=63 19/32"; G=39"; G+((G/5*3)+2")=78 15/16"; G-(G/5*3)=1 1/16"; G-2.5"=36 13/16"; G/10*3=9 1/2"; G/5*3=18 31/32"; H=60 3/4"; H-1.5=59 1/4"; INLET=37 15/16"; INLET/2=18 31/32"; J=32 5/16"; K=57"; L=25 17/32"; M=51 1/16"; M/2=25 17/32"; N=9 5/8"; P=63 11/16"; P-N=-54 1/16"; P-N-M=3"; R=2 3/16"; R+R=4 3/8"; R/2=1 3/32"; S=49 5/16"; T=24 21/32"; Type Comments=Airfoil Centrifugal Blower Counter-Clockwise Bottom Horizontal Arrangement 3 Class 2; U=18"; V=12"; W=13/16"; W/2=13/32"; X=53 7/16"; X/2=26 23/32"
- 330_CA-DWDI_CCW_BHD_CLASS_3: ((B+.25")/2)=23 21/32"; (D-A-.25")/2=2 3/32"; (G/5*3)+2"=20 31/32"; (M-(B+.25"))/2=1 7/8"; -((B+.25")/2)=-23 21/32"; -P=-63 15/16"; A=34 1/2"; A+.25"=34 3/4"; A/2=17 1/4"; B=47 1/16"; B+.25"=47 5/16"; B/2=23 17/32"; BHD_L=3 1/8"; D=38 15/16"; D/2=19 15/32"; E=51 1/2"; E/2=25 3/4"; F=65 13/16"; F-((D-A)/2)=63 19/32"; G=39"; G+((G/5*3)+2")=78 15/16"; G-(G/5*3)=1 1/16"; G-2.5"=36 9/16"; G/10*3=9 1/2"; G/5*3=18 31/32"; H=60 3/4"; H-1.5=59 1/4"; INLET=37 15/16"; INLET/2=18 31/32"; J=32 5/16"; K=57"; L=25 17/32"; M=51 1/16"; M/2=25 17/32"; N=10"; P=63 15/16"; P-N=-53 15/16"; P-N-M=2 7/8"; R=2 7/16"; R+R=4 7/8"; R/2=1 7/32"; S=49 5/16"; T=24 21/32"; Type Comments=Airfoil Centrifugal Blower Counter-Clockwise Bottom Horizontal Arrangement 3 Class 3; U=18"; V=12"; W=13/16"; W/2=13/32"; X=53 7/16"; X/2=26 23/32"
- 365_CA-DWDI_CCW_BHD_CLASS_2: ((B+.25")/2)=26 7/32"; (D-A-.25")/2=2 3/32"; (G/5*3)+2"=22 23/32"; (M-(B+.25"))/2=1 7/8"; -((B+.25")/2)=-26 7/32"; -P=-69 9/16"; A=38 11/16"; A+.25"=38 15/16"; A/2=19 11/32"; B=52 3/16"; B+.25"=52 7/16"; B/2=26 3/32"; BHD_L=3 1/4"; D=43 1/8"; D/2=21 9/16"; E=56 5/8"; E/2=28 5/16"; F=72 5/8"; F-((D-A)/2)=70 13/32"; G=43"; G+((G/5*3)+2")=86 7/16"; G-(G/5*3)=1 9/16"; G-2.5"=40 9/16"; G/10*3=10 3/8"; G/5*3=20 23/32"; H=67"; H-1.5=65 1/2"; INLET=41 7/16"; INLET/2=20 23/32"; J=35 9/16"; K=63"; L=28 3/32"; M=56 3/16"; M/2=28 3/32"; N=10 1/2"; P=69 9/16"; P-N=-59 1/16"; P-N-M=2 7/8"; R=2 7/16"; R+R=4 7/8"; R/2=1 7/32"; S=54 7/16"; T=27 7/32"; Type Comments=Airfoil Centrifugal Blower Counter-Clockwise Bottom Horizontal Arrangement 3 Class 2; U=20"; V=13"; W=13/16"; W/2=13/32"; X=58 9/16"; X/2=29 9/32"
- 365_CA-DWDI_CCW_BHD_CLASS_3: ((B+.25")/2)=26 7/32"; (D-A-.25")/2=2 3/32"; (G/5*3)+2"=22 23/32"; (M-(B+.25"))/2=1 7/8"; -((B+.25")/2)=-26 7/32"; -P=-70 1/16"; A=38 11/16"; A+.25"=38 15/16"; A/2=19 11/32"; B=52 3/16"; B+.25"=52 7/16"; B/2=26 3/32"; BHD_L=3 1/4"; D=43 1/8"; D/2=21 9/16"; E=56 5/8"; E/2=28 5/16"; F=72 5/8"; F-((D-A)/2)=70 13/32"; G=43"; G+((G/5*3)+2")=86 7/16"; G-(G/5*3)=1 9/16"; G-2.5"=40 5/16"; G/10*3=10 3/8"; G/5*3=20 23/32"; H=67"; H-1.5=65 1/2"; INLET=41 7/16"; INLET/2=20 23/32"; J=35 9/16"; K=63"; L=28 3/32"; M=56 3/16"; M/2=28 3/32"; N=10 1/2"; P=70 1/16"; P-N=-59 9/16"; P-N-M=3 3/8"; R=2 11/16"; R+R=5 3/8"; R/2=1 11/32"; S=54 7/16"; T=27 7/32"; Type Comments=Airfoil Centrifugal Blower Counter-Clockwise Bottom Horizontal Arrangement 3 Class 3; U=20"; V=13"; W=13/16"; W/2=13/32"; X=58 9/16"; X/2=29 9/32"
- 402_CA-DWDI_CCW_BHD_CLASS_2: ((B+.25")/2)=29 1/32"; (D-A-.25")/2=2 3/32"; (G/5*3)+2"=24 19/32"; (M-(B+.25"))/2=2 7/8"; -((B+.25")/2)=-29 1/32"; -P=-75 11/16"; A=41 3/4"; A+.25"=42"; A/2=20 7/8"; B=57 13/16"; B+.25"=58 1/16"; B/2=28 29/32"; BHD_L=3 1/4"; D=46 3/16"; D/2=23 3/32"; E=62 1/4"; E/2=31 1/8"; F=79 5/8"; F-((D-A)/2)=77 13/32"; G=47"; G+((G/5*3)+2")=94 3/16"; G-(G/5*3)=1 13/16"; G-2.5"=44 9/16"; G/10*3=11 5/16"; G/5*3=22 19/32"; H=73 7/8"; H-1.5=72 3/8"; INLET=45 3/16"; INLET/2=22 19/32"; J=39 3/16"; K=69"; L=31 29/32"; M=63 13/16"; M/2=31 29/32"; N=10"; P=75 11/16"; P-N=-65 11/16"; P-N-M=1 7/8"; R=2 7/16"; R+R=4 7/8"; R/2=1 7/32"; S=61 5/16"; T=30 21/32"; Type Comments=Airfoil Centrifugal Blower Counter-Clockwise Bottom Horizontal Arrangement 3 Class 2; U=22"; V=14"; W=1 1/16"; W/2=17/32"; X=65 3/16"; X/2=32 19/32"
- 402_CA-DWDI_CCW_BHD_CLASS_3: ((B+.25")/2)=29 1/32"; (D-A-.25")/2=2 3/32"; (G/5*3)+2"=24 19/32"; (M-(B+.25"))/2=2 7/8"; -((B+.25")/2)=-29 1/32"; -P=-76 3/16"; A=41 3/4"; A+.25"=42"; A/2=20 7/8"; B=57 13/16"; B+.25"=58 1/16"; B/2=28 29/32"; BHD_L=3 1/4"; D=46 3/16"; D/2=23 3/32"; E=62 1/4"; E/2=31 1/8"; F=79 5/8"; F-((D-A)/2)=77 13/32"; G=47"; G+((G/5*3)+2")=94 3/16"; G-(G/5*3)=1 13/16"; G-2.5"=44 5/16"; G/10*3=11 5/16"; G/5*3=22 19/32"; H=73 7/8"; H-1.5=72 3/8"; INLET=45 3/16"; INLET/2=22 19/32"; J=39 3/16"; K=69"; L=31 29/32"; M=63 13/16"; M/2=31 29/32"; N=10 1/2"; P=76 3/16"; P-N=-65 11/16"; P-N-M=1 7/8"; R=2 11/16"; R+R=5 3/8"; R/2=1 11/32"; S=61 5/16"; T=30 21/32"; Type Comments=Airfoil Centrifugal Blower Counter-Clockwise Bottom Horizontal Arrangement 3 Class 3; U=22"; V=14"; W=1 1/16"; W/2=17/32"; X=65 3/16"; X/2=32 19/32"
- 445_CA-DWDI_CCW_BHD_CLASS_2: ((B+.25")/2)=32 1/4"; (D-A-.25")/2=2 3/32"; (G/5*3)+2"=26 23/32"; (M-(B+.25"))/2=2 7/8"; -((B+.25")/2)=-32 1/4"; -P=-83 1/2"; A=45 15/16"; A+.25"=46 3/16"; A/2=22 31/32"; B=64 1/4"; B+.25"=64 1/2"; B/2=32 1/8"; BHD_L=3 5/8"; D=50 3/8"; D/2=25 3/16"; E=68 11/16"; E/2=34 11/32"; F=88 1/8"; F-((D-A)/2)=85 29/32"; G=52"; G+((G/5*3)+2")=103 7/16"; G-(G/5*3)=2 9/16"; G-2.5"=49 5/16"; G/10*3=12 3/8"; G/5*3=24 23/32"; H=81 1/2"; H-1.5=80"; INLET=49 7/16"; INLET/2=24 23/32"; J=43 3/16"; K=77"; L=35 1/8"; M=70 1/4"; M/2=35 1/8"; N=11"; P=83 1/2"; P-N=-72 1/2"; P-N-M=2 1/4"; R=2 11/16"; R+R=5 3/8"; R/2=1 11/32"; S=67 3/4"; T=33 7/8"; Type Comments=Airfoil Centrifugal Blower Counter-Clockwise Bottom Horizontal Arrangement 3 Class 2; U=24"; V=16"; W=1 1/16"; W/2=17/32"; X=71 5/8"; X/2=35 13/16"
- 445_CA-DWDI_CCW_BHD_CLASS_3: ((B+.25")/2)=32 1/4"; (D-A-.25")/2=2 3/32"; (G/5*3)+2"=26 23/32"; (M-(B+.25"))/2=2 7/8"; -((B+.25")/2)=-32 1/4"; -P=-83 1/2"; A=45 15/16"; A+.25"=46 3/16"; A/2=22 31/32"; B=64 1/4"; B+.25"=64 1/2"; B/2=32 1/8"; BHD_L=3 5/8"; D=50 3/8"; D/2=25 3/16"; E=68 11/16"; E/2=34 11/32"; F=88 1/8"; F-((D-A)/2)=85 29/32"; G=52"; G+((G/5*3)+2")=103 7/16"; G-(G/5*3)=2 9/16"; G-2.5"=49 1/16"; G/10*3=12 3/8"; G/5*3=24 23/32"; H=81 1/2"; H-1.5=80"; INLET=49 7/16"; INLET/2=24 23/32"; J=43 3/16"; K=77"; L=35 1/8"; M=70 1/4"; M/2=35 1/8"; N=11"; P=83 1/2"; P-N=-72 1/2"; P-N-M=2 1/4"; R=2 15/16"; R+R=5 7/8"; R/2=1 15/32"; S=67 3/4"; T=33 7/8"; Type Comments=Airfoil Centrifugal Blower Counter-Clockwise Bottom Horizontal Arrangement 3 Class 3; U=24"; V=16"; W=1 1/16"; W/2=17/32"; X=71 5/8"; X/2=35 13/16"
- 490_CA-DWDI_CCW_BHD_CLASS_2: ((B+.25")/2)=35 3/16"; (D-A-.25")/2=2 3/32"; (G/5*3)+2"=29 1/2"; (M-(B+.25"))/2=2 7/8"; -((B+.25")/2)=-35 3/16"; -P=-90 3/8"; A=51"; A+.25"=51 1/4"; A/2=25 1/2"; B=70 1/8"; B+.25"=70 3/8"; B/2=35 1/16"; BHD_L=3 3/4"; D=55 7/16"; D/2=27 23/32"; E=74 9/16"; E/2=37 9/32"; F=96 3/4"; F-((D-A)/2)=94 17/32"; G=57"; G+((G/5*3)+2")=114"; G-(G/5*3)=2"; G-2.5"=53 9/16"; G/10*3=13 3/4"; G/5*3=27 1/2"; H=89 3/4"; H-1.5=88 1/4"; INLET=55"; INLET/2=27 1/2"; J=47 9/16"; K=85"; L=38 1/16"; M=76 1/8"; M/2=38 1/16"; N=12"; P=90 3/8"; P-N=-78 3/8"; P-N-M=2 1/4"; R=3 7/16"; R+R=6 7/8"; R/2=1 23/32"; S=73 5/8"; T=36 13/16"; Type Comments=Airfoil Centrifugal Blower Counter-Clockwise Bottom Horizontal Arrangement 3 Class 2; U=26 1/2"; V=18"; W=1 1/16"; W/2=17/32"; X=77 1/2"; X/2=38 3/4"
- 490_CA-DWDI_CCW_BHD_CLASS_3: ((B+.25")/2)=35 3/16"; (D-A-.25")/2=2 3/32"; (G/5*3)+2"=29 1/2"; (M-(B+.25"))/2=2 7/8"; -((B+.25")/2)=-35 3/16"; -P=-90 5/8"; A=51"; A+.25"=51 1/4"; A/2=25 1/2"; B=70 1/8"; B+.25"=70 3/8"; B/2=35 1/16"; BHD_L=3 3/4"; D=55 7/16"; D/2=27 23/32"; E=74 9/16"; E/2=37 9/32"; F=96 3/4"; F-((D-A)/2)=94 17/32"; G=57"; G+((G/5*3)+2")=114"; G-(G/5*3)=2"; G-2.5"=53 9/16"; G/10*3=13 3/4"; G/5*3=27 1/2"; H=89 3/4"; H-1.5=88 1/4"; INLET=55"; INLET/2=27 1/2"; J=47 9/16"; K=85"; L=38 1/16"; M=76 1/8"; M/2=38 1/16"; N=12"; P=90 5/8"; P-N=-78 5/8"; P-N-M=2 1/2"; R=3 7/16"; R+R=6 7/8"; R/2=1 23/32"; S=73 5/8"; T=36 13/16"; Type Comments=Airfoil Centrifugal Blower Counter-Clockwise Bottom Horizontal Arrangement 3 Class 3; U=26 1/2"; V=18"; W=1 1/16"; W/2=17/32"; X=77 1/2"; X/2=38 3/4"
- 540_CA-DWDI_CCW_BHD_CLASS_2: ((B+.25")/2)=39 3/32"; (D-A-.25")/2=2 3/32"; (G/5*3)+2"=32"; (M-(B+.25"))/2=2 7/8"; -((B+.25")/2)=-39 3/32"; -P=-99 15/16"; A=55 3/4"; A+.25"=56"; A/2=27 7/8"; B=77 15/16"; B+.25"=78 3/16"; B/2=38 31/32"; BHD_L=3 1/4"; D=60 3/16"; D/2=30 3/32"; E=82 3/8"; E/2=41 3/16"; F=105 13/16"; F-((D-A)/2)=103 19/32"; G=62"; G+((G/5*3)+2")=124"; G-(G/5*3)=2"; G-2.5"=58 1/16"; G/10*3=15"; G/5*3=30"; H=98 3/4"; H-1.5=97 1/4"; INLET=60"; INLET/2=30"; J=52 1/4"; K=94"; L=41 31/32"; M=83 15/16"; M/2=41 31/32"; N=13 3/4"; P=99 15/16"; P-N=-86 3/16"; P-N-M=2 1/4"; R=3 15/16"; R+R=7 7/8"; R/2=1 31/32"; S=81 7/16"; T=40 23/32"; Type Comments=Airfoil Centrifugal Blower Counter-Clockwise Bottom Horizontal Arrangement 3 Class 2; U=29"; V=20"; W=1 1/16"; W/2=17/32"; X=88 5/16"; X/2=44 5/32"
- 540_CA-DWDI_CCW_BHD_CLASS_3: ((B+.25")/2)=39 3/32"; (D-A-.25")/2=2 3/32"; (G/5*3)+2"=32"; (M-(B+.25"))/2=2 7/8"; -((B+.25")/2)=-39 3/32"; -P=-100 3/16"; A=55 3/4"; A+.25"=56"; A/2=27 7/8"; B=77 15/16"; B+.25"=78 3/16"; B/2=38 31/32"; BHD_L=3 1/4"; D=60 3/16"; D/2=30 3/32"; E=82 3/8"; E/2=41 3/16"; F=105 13/16"; F-((D-A)/2)=103 19/32"; G=62"; G+((G/5*3)+2")=124"; G-(G/5*3)=2"; G-2.5"=58 1/16"; G/10*3=15"; G/5*3=30"; H=98 3/4"; H-1.5=97 1/4"; INLET=60"; INLET/2=30"; J=52 1/4"; K=94"; L=41 31/32"; M=83 15/16"; M/2=41 31/32"; N=14 3/16"; P=100 3/16"; P-N=-86"; P-N-M=2 1/16"; R=3 15/16"; R+R=7 7/8"; R/2=1 31/32"; S=81 7/16"; T=40 23/32"; Type Comments=Airfoil Centrifugal Blower Counter-Clockwise Bottom Horizontal Arrangement 3 Class 3; U=29"; V=20"; W=1 1/16"; W/2=17/32"; X=88 5/16"; X/2=44 5/32"
- 600_CA-DWDI_CCW_BHD_CLASS_2: ((B+.25")/2)=43 1/4"; (D-A-.25")/2=2 3/32"; (G/5*3)+2"=35"; (M-(B+.25"))/2=2 7/8"; -((B+.25")/2)=-43 1/4"; -P=-108 3/4"; A=62 3/16"; A+.25"=62 7/16"; A/2=31 3/32"; B=86 1/4"; B+.25"=86 1/2"; B/2=43 1/8"; BHD_L=3 3/4"; D=66 5/8"; D/2=33 5/16"; E=90 11/16"; E/2=45 11/32"; F=117 11/16"; F-((D-A)/2)=115 15/32"; G=69"; G+((G/5*3)+2")=137"; G-(G/5*3)=3"; G-2.5"=65 1/16"; G/10*3=16 1/2"; G/5*3=33"; H=109 5/8"; H-1.5=108 1/8"; INLET=66"; INLET/2=33"; J=57 15/16"; K=105"; L=46 1/8"; M=92 1/4"; M/2=46 1/8"; N=14 1/4"; P=108 3/4"; P-N=-94 1/2"; P-N-M=2 1/4"; R=3 15/16"; R+R=7 7/8"; R/2=1 31/32"; S=89 3/4"; T=44 7/8"; Type Comments=Airfoil Centrifugal Blower Counter-Clockwise Bottom Horizontal Arrangement 3 Class 2; U=32"; V=22"; W=1 1/16"; W/2=17/32"; X=96 5/8"; X/2=48 5/16"
- 600_CA-DWDI_CCW_BHD_CLASS_3: ((B+.25")/2)=43 1/4"; (D-A-.25")/2=2 3/32"; (G/5*3)+2"=35"; (M-(B+.25"))/2=2 7/8"; -((B+.25")/2)=-43 1/4"; -P=-110 3/4"; A=62 3/16"; A+.25"=62 7/16"; A/2=31 3/32"; B=86 1/4"; B+.25"=86 1/2"; B/2=43 1/8"; BHD_L=3 3/4"; D=66 5/8"; D/2=33 5/16"; E=90 11/16"; E/2=45 11/32"; F=117 11/16"; F-((D-A)/2)=115 15/32"; G=69"; G+((G/5*3)+2")=137"; G-(G/5*3)=3"; G-2.5"=64 9/16"; G/10*3=16 1/2"; G/5*3=33"; H=109 5/8"; H-1.5=108 1/8"; INLET=66"; INLET/2=33"; J=57 15/16"; K=105"; L=46 1/8"; M=92 1/4"; M/2=46 1/8"; N=14 3/4"; P=110 3/4"; P-N=-96"; P-N-M=3 3/4"; R=4 7/16"; R+R=8 7/8"; R/2=2 7/32"; S=89 3/4"; T=44 7/8"; Type Comments=Airfoil Centrifugal Blower Counter-Clockwise Bottom Horizontal Arrangement 3 Class 3; U=32"; V=22"; W=1 1/16"; W/2=17/32"; X=96 5/8"; X/2=48 5/16"
- 660_CA-DWDI_CCW_BHD_CLASS_2: ((B+.25")/2)=47 9/16"; (D-A-.25")/2=2 3/32"; (G/5*3)+2"=38"; (M-(B+.25"))/2=2 7/8"; -((B+.25")/2)=-47 9/16"; -P=-118 5/8"; A=68 7/16"; A+.25"=68 11/16"; A/2=34 7/32"; B=94 7/8"; B+.25"=95 1/8"; B/2=47 7/16"; BHD_L=3 1/4"; D=72 7/8"; D/2=36 7/16"; E=99 5/16"; E/2=49 21/32"; F=128 9/16"; F-((D-A)/2)=126 11/32"; G=75"; G+((G/5*3)+2")=149"; G-(G/5*3)=3"; G-2.5"=70 9/16"; G/10*3=18"; G/5*3=36"; H=120 5/8"; H-1.5=119 1/8"; INLET=72"; INLET/2=36"; J=63 3/4"; K=116"; L=50 7/16"; M=100 7/8"; M/2=50 7/16"; N=15 5/16"; P=118 5/8"; P-N=-103 5/16"; P-N-M=2 7/16"; R=4 7/16"; R+R=8 7/8"; R/2=2 7/32"; S=98 3/8"; T=49 3/16"; Type Comments=Airfoil Centrifugal Blower Counter-Clockwise Bottom Horizontal Arrangement 3 Class 2; U=35"; V=25"; W=1 1/16"; W/2=17/32"; X=105 1/4"; X/2=52 5/8"
- 660_CA-DWDI_CCW_BHD_CLASS_3: ((B+.25")/2)=47 9/16"; (D-A-.25")/2=2 3/32"; (G/5*3)+2"=38"; (M-(B+.25"))/2=2 7/8"; -((B+.25")/2)=-47 9/16"; -P=-119 7/8"; A=68 7/16"; A+.25"=68 11/16"; A/2=34 7/32"; B=94 7/8"; B+.25"=95 1/8"; B/2=47 7/16"; BHD_L=3 1/4"; D=72 7/8"; D/2=36 7/16"; E=99 5/16"; E/2=49 21/32"; F=128 9/16"; F-((D-A)/2)=126 11/32"; G=75"; G+((G/5*3)+2")=149"; G-(G/5*3)=3"; G-2.5"=70 9/16"; G/10*3=18"; G/5*3=36"; H=120 5/8"; H-1.5=119 1/8"; INLET=72"; INLET/2=36"; J=63 3/4"; K=116"; L=50 7/16"; M=100 7/8"; M/2=50 7/16"; N=14 5/8"; P=119 7/8"; P-N=-105 1/4"; P-N-M=4 3/8"; R=4 7/16"; R+R=8 7/8"; R/2=2 7/32"; S=98 3/8"; T=49 3/16"; Type Comments=Airfoil Centrifugal Blower Counter-Clockwise Bottom Horizontal Arrangement 3 Class 3; U=35"; V=25"; W=1 1/16"; W/2=17/32"; X=105 1/4"; X/2=52 5/8"
- 730 _CA-DWDI_CCW_BHD_CLASS_2: ((B+.25")/2)=52 1/2"; (D-A-.25")/2=2 3/32"; (G/5*3)+2"=41 1/2"; (M-(B+.25"))/2=2 7/8"; -((B+.25")/2)=-52 1/2"; -P=-130 3/4"; A=75 13/16"; A+.25"=76 1/16"; A/2=37 29/32"; B=104 3/4"; B+.25"=105"; B/2=52 3/8"; BHD_L=3 5/8"; D=80 1/4"; D/2=40 1/8"; E=109 3/16"; E/2=54 19/32"; F=142 1/4"; F-((D-A)/2)=140 1/32"; G=83"; G+((G/5*3)+2")=164"; G-(G/5*3)=4"; G-2.5"=78 9/16"; G/10*3=19 3/4"; G/5*3=39 1/2"; H=133 1/4"; H-1.5=131 3/4"; INLET=79"; INLET/2=39 1/2"; J=70 3/8"; K=129"; L=55 3/8"; M=110 3/4"; M/2=55 3/8"; N=16 1/4"; P=130 3/4"; P-N=-114 1/2"; P-N-M=3 3/4"; R=4 7/16"; R+R=8 7/8"; R/2=2 7/32"; S=108 1/4"; T=54 1/8"; Type Comments=Airfoil Centrifugal Blower Counter-Clockwise Bottom Horizontal Arrangement 3 Class 2; U=38 1/2"; V=28"; W=1 1/16"; W/2=17/32"; X=115 1/8"; X/2=57 9/16"
- 730 _CA-DWDI_CCW_BHD_CLASS_3: ((B+.25")/2)=52 1/2"; (D-A-.25")/2=2 3/32"; (G/5*3)+2"=41 1/2"; (M-(B+.25"))/2=2 7/8"; -((B+.25")/2)=-52 1/2"; -P=-131 1/4"; A=75 13/16"; A+.25"=76 1/16"; A/2=37 29/32"; B=104 3/4"; B+.25"=105"; B/2=52 3/8"; BHD_L=3 5/8"; D=80 1/4"; D/2=40 1/8"; E=109 3/16"; E/2=54 19/32"; F=142 1/4"; F-((D-A)/2)=140 1/32"; G=83"; G+((G/5*3)+2")=164"; G-(G/5*3)=4"; G-2.5"=78 1/16"; G/10*3=19 3/4"; G/5*3=39 1/2"; H=133 1/4"; H-1.5=131 3/4"; INLET=79"; INLET/2=39 1/2"; J=70 3/8"; K=129"; L=55 3/8"; M=110 3/4"; M/2=55 3/8"; N=16 3/4"; P=131 1/4"; P-N=-114 1/2"; P-N-M=3 3/4"; R=4 15/16"; R+R=9 7/8"; R/2=2 15/32"; S=108 1/4"; T=54 1/8"; Type Comments=Airfoil Centrifugal Blower Counter-Clockwise Bottom Horizontal Arrangement 3 Class 3; U=38 1/2"; V=28"; W=1 1/16"; W/2=17/32"; X=115 1/8"; X/2=57 9/16"

## geometry (parser evidence)
native form markers: Sweep x3
no freeform markers — native parametric forms only
